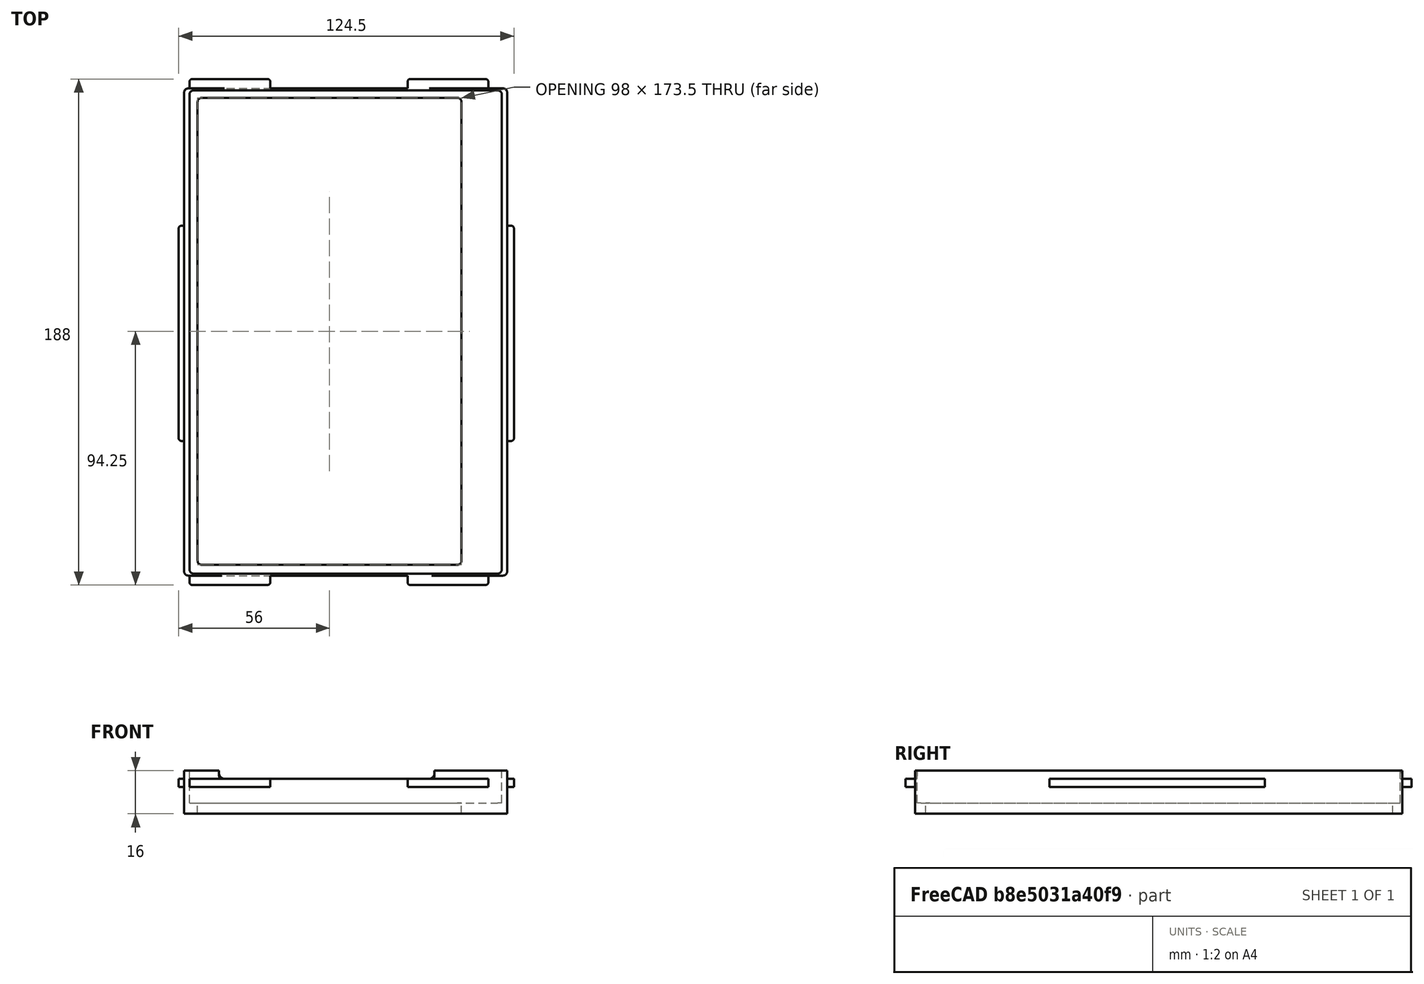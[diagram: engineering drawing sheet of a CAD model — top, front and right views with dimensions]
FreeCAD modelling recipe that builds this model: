
FCSTD DOCUMENT  (FreeCAD 0.20R29177 (Git))
Label: carrier-atoto-s8_test_h
License: All rights reserved
LicenseURL: http://en.wikipedia.org/wiki/All_rights_reserved
objects: Part::Box×12, Part::Fillet×11, Part::MultiFuse×4, Part::Cut×3
note: 30 computed .brp shape members not serialized (recipe doc carries the construction recipe); baked Part::Feature solids carry a one-line shape summary decoded from their .brp

FEATURE [Part::Box] Box  label="Cube"
  AttacherType = Attacher::AttachEngine3D
  Height = 4
  Length = 120
  Placement = pos=(2,0,0) rot=(0,0,1;0rad)
  Width = 181
FEATURE [Part::Box] Box001  label="Cube001"
  AttacherType = Attacher::AttachEngine3D
  Height = 4
  Length = 98
  Placement = pos=(7,4,0) rot=(0,0,1;0rad)
  Width = 173.5
FEATURE [Part::Fillet] Fillet
  Base = -> Box001
  Edges = 4 edges r=1.5: [Edge1,Edge3,Edge5,Edge7]
FEATURE [Part::Fillet] Fillet001
  Base = -> Box
  Edges = 4 edges r=1.5: [Edge1,Edge3,Edge5,Edge7]
FEATURE [Part::Cut] Cut
  Base = -> Fillet001
  Tool = -> Fillet
FEATURE [Part::Box] Box002  label="Cube002"
  AttacherType = Attacher::AttachEngine3D
  Height = 12
  Length = 120
  Placement = pos=(2,0,4) rot=(0,0,1;0rad)
  Width = 181
FEATURE [Part::Box] Box003  label="Cube003"
  AttacherType = Attacher::AttachEngine3D
  Height = 20
  Length = 116
  Placement = pos=(4,0.75,4) rot=(0,0,1;0rad)
  Width = 179.5
FEATURE [Part::Fillet] Fillet002
  Base = -> Box003
  Edges = 4 edges r=1.5: [Edge1,Edge3,Edge5,Edge7]
FEATURE [Part::Fillet] Fillet003
  Base = -> Box002
  Edges = 4 edges r=1.5: [Edge1,Edge3,Edge5,Edge7]
FEATURE [Part::Cut] Cut001
  Base = -> Fillet003
  Tool = -> Fillet002
FEATURE [Part::Box] Box006  label="Cube006"
  AttacherType = Attacher::AttachEngine3D
  Height = 10
  Length = 80
  Placement = pos=(15,-5,0) rot=(0,0,1;0rad)
  Width = 10
FEATURE [Part::Box] Box007  label="Cube007"
  AttacherType = Attacher::AttachEngine3D
  Height = 10
  Length = 80
  Placement = pos=(15,175,0) rot=(0,0,1;0rad)
  Width = 10
FEATURE [Part::MultiFuse] Fusion
  Placement = pos=(0,0,13) rot=(0,0,1;0rad)
  Shapes = -> [Box007,Box006]
FEATURE [Part::Fillet] Fillet004
  Base = -> Fusion
  Edges = 4 edges: [Edge4 r=2,Edge8 r=2,Edge16 r=1,Edge20 r=1]
FEATURE [Part::Cut] Cut002
  Base = -> Cut001
  Tool = -> Fillet004
FEATURE [Part::MultiFuse] Fusion001
  Shapes = -> [Cut,Cut002]
FEATURE [Part::Box] Box008  label="Cube008"
  AttacherType = Attacher::AttachEngine3D
  Height = 3
  Length = 30
  Placement = pos=(85,180.5,5) rot=(0,0,1;0rad)
  Width = 4
FEATURE [Part::Box] Box009  label="Cube009"
  AttacherType = Attacher::AttachEngine3D
  Height = 3
  Length = 30
  Placement = pos=(4,180.5,5) rot=(0,0,1;0rad)
  Width = 4
FEATURE [Part::Box] Box010  label="Cube010"
  AttacherType = Attacher::AttachEngine3D
  Height = 3
  Length = 30
  Placement = pos=(85,-3.5,5) rot=(0,0,1;0rad)
  Width = 4
FEATURE [Part::Box] Box011  label="Cube011"
  AttacherType = Attacher::AttachEngine3D
  Height = 3
  Length = 4
  Placement = pos=(0,50,5) rot=(0,0,1;0rad)
  Width = 80
FEATURE [Part::Box] Box012  label="Cube012"
  AttacherType = Attacher::AttachEngine3D
  Height = 3
  Length = 30
  Placement = pos=(4,-3.5,5) rot=(0,0,1;0rad)
  Width = 4
FEATURE [Part::Box] Box013  label="Cube013"
  AttacherType = Attacher::AttachEngine3D
  Height = 3
  Length = 4
  Placement = pos=(120.5,50,5) rot=(0,0,1;0rad)
  Width = 80
FEATURE [Part::Fillet] Fillet005
  Base = -> Box012
  Edges = 2 edges r=1: [Edge1,Edge5]
FEATURE [Part::Fillet] Fillet006
  Base = -> Box011
  Edges = 2 edges r=1: [Edge1,Edge3]
FEATURE [Part::Fillet] Fillet007
  Base = -> Box010
  Edges = 2 edges r=1: [Edge1,Edge5]
FEATURE [Part::Fillet] Fillet008
  Base = -> Box009
  Edges = 2 edges r=1: [Edge3,Edge7]
FEATURE [Part::Fillet] Fillet009
  Base = -> Box008
  Edges = 2 edges r=1: [Edge3,Edge7]
FEATURE [Part::Fillet] Fillet010
  Base = -> Box013
  Edges = 2 edges r=1: [Edge5,Edge7]
FEATURE [Part::MultiFuse] Fusion002
  Placement = pos=(0,0,5) rot=(0,0,1;0rad)
  Shapes = -> [Fillet005,Fillet006,Fillet007,Fillet008,Fillet009,Fillet010]
FEATURE [Part::MultiFuse] Fusion003
  Shapes = -> [Fusion001,Fusion002]
